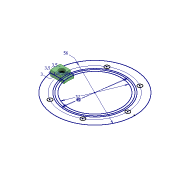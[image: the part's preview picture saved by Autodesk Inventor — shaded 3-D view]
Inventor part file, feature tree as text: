
AUTODESK INVENTOR PART (.ipt)
format: ipt  version: 2020.3 (Build 243373000, 373)  size: 101,888 bytes
history: native  units: mm
features: extrude x2, sketch x1
ambient origin geometry x8: Origin, YZ Plane, XZ Plane, XY Plane, X Axis, Y Axis, Z Axis, Center Point
bodies: Solid1 (feature_tree)
feature tree (3):
  sketch  "Sketch2"  dims[d7=60.0mm d8=37.0mm d9=3.0mm d10=360.0deg d11=56.0mm d12=40.0mm d13=42.0mm d14=3.5mm d15=3.5mm d16=4.0mm d17=1.8mm d18=0.0mm d19=2.0mm d20=0.0mm]
  extrude  "Extrusion1"  Depth=2.0mm
  extrude  "Extrusion2"  Depth=2.0mm
